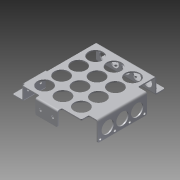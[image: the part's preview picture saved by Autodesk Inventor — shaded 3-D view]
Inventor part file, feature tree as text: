
AUTODESK INVENTOR PART (.ipt)
format: ipt  version: 2013 (Build 170138000, 138)  size: 632,832 bytes
history: native  units: in
note: dims shown in document units (in); Inventor stores cm internally (conversion verified against a paired STEP export)
features: sheet_metal_op x21, other x15, sketch x13, chamfer x2, reference x2
ambient origin geometry x8: Origin, YZ Plane, XZ Plane, XY Plane, X Axis, Y Axis, Z Axis, Center Point
bodies: Solid1 (feature_tree)
feature tree (53):
  sheet_metal_op  "Face1"
  sheet_metal_op  "Flange1"
  sheet_metal_op  "Flange2"
  sketch  "Sketch4"  dims[d3=0.5in]
  sheet_metal_op  "Face2"
  sheet_metal_op  "Flange3"
  sheet_metal_op  "Flange4"
  chamfer  "Corner Round1"
  sheet_metal_op  "Flange5"
  sheet_metal_op  "Flange6"
  chamfer  "Corner Round2"
  sketch  "Sketch1"  dims[d0=1.0in]
  other  "Plate1"
  sketch  "Sketch2"  dims[d1=6.0in]
  other  "Plate2"
  sheet_metal_op  "Bend1"
  sheet_metal_op  "Corner1"
  sketch  "Sketch3"  dims[d2=0.26in]
  other  "Plate3"
  sheet_metal_op  "Bend2"
  sheet_metal_op  "Corner2"
  other  "Plate4"
  sheet_metal_op  "Bend3"
  sketch  "Sketch5"  dims[d4=2.3622in d6=1.0in d7=0.3937in d9=1.0in]
  other  "Plate5"
  sheet_metal_op  "Bend4"
  sheet_metal_op  "Corner3"
  sketch  "Sketch6"  dims[d11=0.5in]
  other  "Plate6"
  sheet_metal_op  "Bend5"
  sheet_metal_op  "Corner4"
  sketch  "Sketch7"  dims[d12=0.125in]
  sketch  "Sketch8"  dims[d13=0.125in]
  sketch  "Sketch9"  dims[d14=0.0625in]
  other  "Plate7"
  sheet_metal_op  "Bend6"
  sheet_metal_op  "Corner5"
  sketch  "Sketch10"  dims[d15=0.25in]
  other  "Plate8"
  sheet_metal_op  "Bend7"
  sheet_metal_op  "Corner6"
  reference  "Reference10"
  reference  "Reference11"
  sketch  "Sketch11"  dims[d16=0.125in]
  sketch  "Sketch12"  dims[d17=1.5in d18=90.0deg d19=0.05in]
  sketch  "Sketch13"  dims[d20=0.5in d21=0.125in d22=0.125in d23=0.125in d24=0.0625in d25=0.25in d26=0.125in d27=7.625in d28=90.0deg d29=0.05in d30=0.5in d31=0.125in d32=0.125in d33=2.25in d35=0.25in d36=0.125in d37=0.125in d38=0.0625in d39=0.25in d40=0.125in d41=0.125in d42=0.0625in d43=0.25in d44=0.125in d45=1.625in d46=90.0deg d47=0.05in d48=0.5in d49=0.125in d50=0.125in d51=0.125in d52=0.0625in d53=0.25in d54=0.125in d55=1.125in d56=90.0deg d57=0.05in d58=0.5in d59=0.125in d60=0.125in d61=0.125in d62=0.0in d63=0.125in d64=1.5in d65=1.125in d66=1.125in d67=1.5748in d69=1.7333in d70=1.1811in d72=1.875in d75=1.125in d76=1.125in d77=0.125in d78=0.0in d79=0.875in d83=0.75in d84=6.0in d85=1.9685in d87=1.125in d88=0.3937in d90=1.0in d92=0.125in d93=0.0in d95=5.0in d96=0.125in d97=0.0625in d98=0.25in d99=0.125in d100=2.0in d101=90.0deg d102=0.05in d103=0.5in d104=0.125in d105=0.125in d106=0.25in d107=2.25in d108=2.0in d109=0.125in d110=0.0625in d111=0.25in d112=0.125in d113=1.5in d114=90.0deg d115=0.05in d116=0.5in d117=0.125in d118=0.125in d119=0.75in d120=0.75in d121=0.25in d122=5.0in d123=1.25in d124=1.0in d125=1.1811in d127=1.5in d128=0.3937in d130=1.0in d132=1.0in d133=0.25in d134=0.26in d135=0.25in d136=1.5748in d138=1.5in d139=0.3937in d141=1.0in d143=0.25in d144=0.125in d145=0.0in d146=7.45in d147=0.26in d149=0.5in d150=0.5in d151=0.125in d152=0.0in d153=0.26in d155=0.5in d156=0.5in d157=0.125in d158=0.0in d159=0.125in d5=0.0312in d8=0.0625in d10=0.0312in]
  other  "Cut1"
  other  "Cut2"
  other  "Cut3"
  other  "Cut4"
  other  "Cut5"
  other  "Cut6"
  other  "Definition1"
